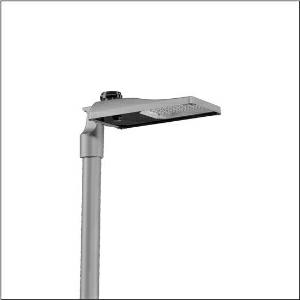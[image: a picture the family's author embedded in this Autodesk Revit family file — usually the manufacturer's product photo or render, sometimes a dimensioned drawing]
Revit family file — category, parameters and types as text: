
# Revit family: streetlight_sl_31_mini___p1_0a_5xh2a35m08ha_3b1d
name_source: partatom
category: Lighting Fixtures
units: mm (PartAtom-declared; Revit-internal decimal feet)

## family parameters
Cut with Voids When Loaded = No
Host = Face
Light Source = No
Part Type = Normal
Room Calculation Point = No
Round Connector Dimension = Use Diameter
Shared = No

## types (1)
- --- (1 x LED, 8970 lm, 68.3 W, 3000K)
    Apparent Load = 68 VA
    CIE Flux Codes = 23 55 94 100 100
    Color Rendering = 70
    Color Temperature = 3000K
    Default Elevation = 1800 mm
    Description = Streetlight SL 31 mini NEMA (7pin), Desk-Remote mast luminaire for post-top, side-entry; light control with lens of PMMA; light distribution: P1.0a, direct asymmetric distribution, for standard-compliant lighting for roads and squares; LED: luminous flux: 8.970lm, light colour: 730, colour temperature: 3000K; luminous efficacy: 131,3lm/W; control: pre-setting: linear dimming characteristic, flexible luminous flux parameterisation, time-dependent luminous flux control, constant luminous flux control, intelligent temperature release in ECG and LED module, overheat protection; luminaire housing, of diecast aluminium, SITECO metallic grey (DB 702S), corrosivity category C5 high according to DIN EN ISO 12944; cover of toughened safety glass, transparent, mast flange of diecast aluminium, SITECO metallic grey (DB 702S), spigot size: 76/60mm, mast flange included unmounted; with cable H07RN-F 3x 1.5mm², cable length: 8,5m, connection cable pre-assembled; mains connection: 220..240V, AC, 50/60Hz; power consumption (at start of service life): 68,3W / (at end of service life): 74,5W / (with reduced operation 50%): 29,5W; protection rating (complete): IP66; insulation class (complete): insulation class I (protective earthing); impact resistance: IK09; certification: CE, ENEC, ENEC+, VDE, UKCA; permissible operating ambient temperature for outdoor applications: -40..+50°C; packaging unit: 1 piece

Light Distribution: P1.0a
    Height = 76 mm
    Lamp = 1 x LED
    Lamp Light Flux = 8970 lm
    Lamp Power = 68.3 W
    Lamp count = 1
    Length = 547 mm
    Luminous efficacy = 131 lm/W
    Manufacturer = Siteco
    ModVariant = No
    Model = 5XH2A35M08HA
    Number of Poles = 1
    OnlyDefault = Yes
    Power Factor = 1
    Product Name = Streetlight SL 31 mini | P1.0a
    Product group = mast luminaire | pylon top
    ProductGroupID = 6100
    Protection Class = Protection class I
    Protection Degree = IP 66
    RLX_Detail_Level = 1
    RLX_Emergency_Light_Flux = 0 lm
    RLX_Emergency_Type = 0
    RLX_Emergency_Type_DB = No
    RlxData = <blob elided: 39709 chars, md5=fce80a78>
    Socket = socket
    Standby Power = 0 W
    System Light Flux = 8970 lm
    System Power = 68 W
    Type Comments = factory setting: luminous flux: 100 % | dim-lin: 254 | 692 mA
    Type Image = l_1300324.jpg
    URL = http://relux.com
    VarID = @adj_027451
    Voltage = 0 V
    Weight = 0.00 kg
    Width = 265 mm

## geometry (parser evidence)
native form markers: Blend x4, Sweep x10
no freeform markers — native parametric forms only
